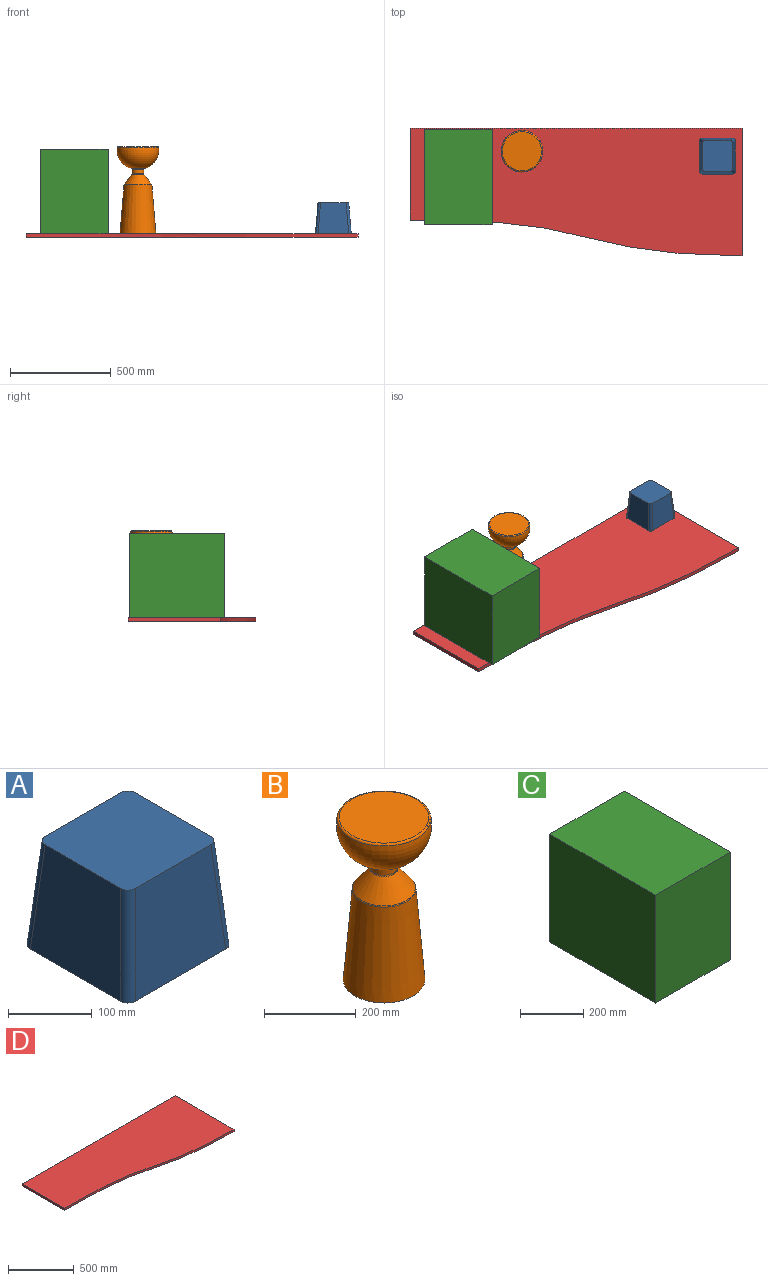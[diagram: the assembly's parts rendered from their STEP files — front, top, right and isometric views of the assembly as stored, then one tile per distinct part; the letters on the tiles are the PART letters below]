
ASSEMBLY  parts=4 mates=3
PART A: 10 faces, bbox 177.9x177.9x153.3 mm
  f0: plane 152.4x152.4mm, normal (0,0,1), area 23088.6mm2, adj f2,f3,f4,f5,f6,f7,f8,f9
  f1: plane 177.8x177.8mm, normal (0,0,-1), area 31475.7mm2, adj f2,f3,f4,f5,f6,f7,f8,f9
  f2: plane 152.49x152.4mm, normal (0,-1,0.08), area 21377.5mm2, adj f0,f1,f8,f9
  f3: plane 152.49x152.4mm, normal (-1,0,0.08), area 21377.5mm2, adj f0,f1,f7,f8
  f4: plane 152.49x152.4mm, normal (0,1,0.08), area 21377.5mm2, adj f0,f1,f6,f7
  f5: plane 152.49x152.4mm, normal (1,0,0.08), area 21377.5mm2, adj f0,f1,f6,f9
  f6: cylinder r=12.7mm len=153.26mm, axis (0.08,0.08,-0.99), area 3047.8mm2, adj f0,f1,f4,f5
  f7: cylinder r=12.7mm len=153.26mm, axis (0.08,-0.08,0.99), area 3047.8mm2, adj f0,f1,f3,f4
  f8: cylinder r=12.7mm len=153.26mm, axis (-0.08,-0.08,-0.99), area 3047.8mm2, adj f0,f1,f2,f3
  f9: cylinder r=12.7mm len=153.26mm, axis (-0.08,0.08,0.99), area 3047.8mm2, adj f0,f1,f2,f5
PART B: 10 faces, bbox 221.9x221.9x431.8 mm
  f0: plane 194.81x194.81mm, normal (0,0,1), area 29805.8mm2, adj f9
  f1: plane 177.8x177.8mm, normal (0,0,-1), area 24828.7mm2, adj f2
  f2: cone r=88.9mm half-angle=4.6deg, axis (0,0,-1), area 120435mm2, adj f1,f6
  f3: cone r=69.22mm half-angle=37.2deg, axis (0,0,-1), area 19607.1mm2, adj f6,f7
  f4: cylinder r=28.92mm len=57.85mm, axis (0,0,1), area 3688.7mm2, adj f7,f8
  f5: torus R=11.92mm, axis (0,0,1), area 70605.8mm2, adj f8,f9
  f6: torus R=64.27mm, axis (0,0,-1), area 1249.8mm2, adj f2,f3
  f7: torus R=34mm, axis (0,0,1), area 606.1mm2, adj f3,f4
  f8: torus R=34mm, axis (0,0,1), area 1297.3mm2, adj f4,f5
  f9: torus R=97.4mm, axis (0,0,1), area 4502.5mm2, adj f0,f5
PART C: 6 faces, bbox 335.3x475x419.1 mm
  f0: plane 419.1x335.28mm, normal (0,1,0), area 140515.8mm2, adj f1,f3,f4,f5
  f1: plane 474.98x419.1mm, normal (-1,0,0), area 199064.1mm2, adj f0,f2,f4,f5
  f2: plane 419.1x335.28mm, normal (0,-1,0), area 140515.8mm2, adj f1,f3,f4,f5
  f3: plane 474.98x419.1mm, normal (1,0,0), area 199064.1mm2, adj f0,f2,f4,f5
  f4: plane 474.98x335.28mm, normal (0,0,1), area 159251.3mm2, adj f0,f1,f2,f3
  f5: plane 474.98x335.28mm, normal (0,0,-1), area 159251.3mm2, adj f0,f1,f2,f3
PART D: 6 faces, bbox 1651x635x19.1 mm
  f0: plane 635x19.05mm, normal (1,0,0), area 12096.7mm2, adj f1,f3,f4,f5
  f1: plane 1651x19.05mm, normal (0,1,0), area 31451.5mm2, adj f0,f2,f4,f5
  f2: plane 457.2x19.05mm, normal (-1,0,0), area 8709.7mm2, adj f1,f3,f4,f5
  f3: extruded ~1651x177.8mm, area 31736.8mm2, adj f0,f2,f4,f5
  f4: plane 1651x635mm, normal (0,0,1), area 890376.8mm2, adj f0,f1,f2,f3
  f5: plane 1651x635mm, normal (0,0,-1), area 890376.8mm2, adj f0,f1,f2,f3
PLACE A t=(-78.6,-297.37,-203.04)mm
PLACE B t=(-1050.3,-273.87,39.91)mm
PLACE C t=(-1356.21,-491.7,-203.04)mm
PLACE D t=(-784.32,-211.26,-222.09)mm fixed
MATE planar D.f4 <-> C.f5  axis (0,0,1) through (-722.48,-432.25,-203.04)mm
MATE planar B.f2 <-> D.f4  axis (0,0,-1) through (-1050.3,-273.87,-203.04)mm
MATE planar A.f1 <-> D.f4  axis (0,0,-1) through (-78.6,-297.37,-203.04)mm
